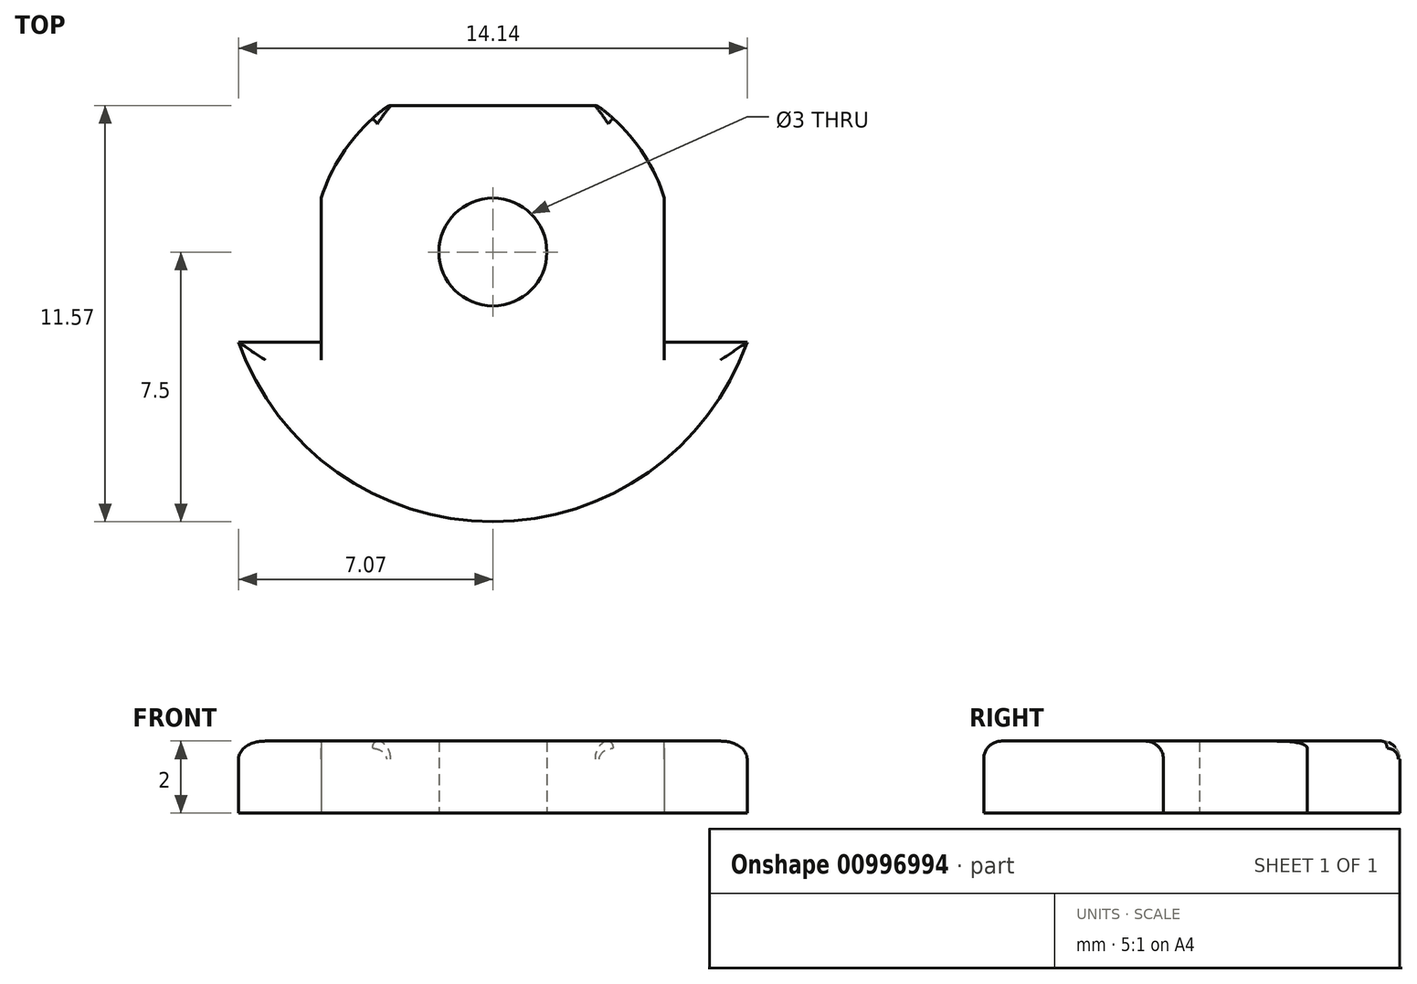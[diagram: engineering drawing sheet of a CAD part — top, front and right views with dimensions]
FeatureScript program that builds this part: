
annotation { "Feature Type Name" : "Feature", "Feature Type Description" : "" }
export const myFeature = defineFeature(function(context is Context, id is Id, definition is map)
    precondition{}
    {
        {
            var Q0;
            Q0=qCreatedBy(makeId("Top.planeOp"),FACE);
            var sketch = newSketch(context, id + "F0", { "sketchPlane" : qUnion([Q0])});
            skCircle(sketch, "E0", {"center": v(0, 0) * mm, "radius": 7.5 * mm});
            skLineSegment(sketch, "E1", {"start": v(-2.7, 7) * mm, "end": v(2.7, 7) * mm});
            skCircle(sketch, "E2", {"center": v(0, 0) * mm, "radius": 5 * mm});
            skLineSegment(sketch, "E3", {"start": v(-2.9, 4.07) * mm, "end": v(2.9, 4.07) * mm});
            skCircle(sketch, "E4", {"center": v(0, 0) * mm, "radius": 1.5 * mm});
            skLineSegment(sketch, "E5", {"start": v(-4.77, 1.5) * mm, "end": v(4.77, 1.5) * mm});
            skLineSegment(sketch, "E6", {"start": v(-7.07, -2.5) * mm, "end": v(7.07, -2.5) * mm});
            skLineSegment(sketch, "E7", {"start": v(-4.77, 1.5) * mm, "end": v(-4.77, -2.5) * mm});
            skLineSegment(sketch, "E8", {"start": v(4.77, 1.5) * mm, "end": v(4.77, -2.5) * mm});
            skSolve(sketch);
        }
        {
            var Q0;
            {var subQ0=sQuery(id+"F0.wireOp",EDGE,"E3");Q0=makeQuery(id+"F0.imprint","IMPRINT",FACE,{"disambiguationData":[TD([[makeQuery(id+"F0.imprint","IMPRINT",EDGE,{"derivedFrom":subQ0}),-1.0]])]});}
            var Q1;
            {var subQ4=sQuery(id+"F0.wireOp",EDGE,"E4");Q1=makeQuery(id+"F0.imprint","IMPRINT",FACE,{"disambiguationData":[TD([[makeQuery(id+"F0.imprint","IMPRINT",EDGE,{"derivedFrom":subQ4}),-1.0]])]});}
            var Q2;
            {var subQ0=sQuery(id+"F0.wireOp",EDGE,"E7");var subQ1=sQuery(id+"F0.wireOp",EDGE,"E2");var subQ2=makeQuery(id+"F0.imprint","INTERSECT",VERTEX,{"derivedFrom":[subQ1,subQ0]});Q2=makeQuery(id+"F0.imprint","IMPRINT",FACE,{"disambiguationData":[TD([[makeQuery(id+"F0.imprint","IMPRINT",EDGE,{"disambiguationData":[TD([[subQ2,-1.0]])],"derivedFrom":subQ1}),-1.0]])]});}
            var Q3;
            {var subQ0=sQuery(id+"F0.wireOp",EDGE,"E6");var subQ1=sQuery(id+"F0.wireOp",EDGE,"E2");var subQ2=makeQuery(id+"F0.imprint","INTERSECT",VERTEX,{"disambiguationData":[OD(0.0)],"derivedFrom":[subQ1,subQ0]});Q3=makeQuery(id+"F0.imprint","IMPRINT",FACE,{"disambiguationData":[TD([[makeQuery(id+"F0.imprint","IMPRINT",EDGE,{"disambiguationData":[TD([[subQ2,-1.0]])],"derivedFrom":subQ1}),1.0]])]});}
            var Q4;
            {var subQ0=sQuery(id+"F0.wireOp",EDGE,"E6");var subQ5=sQuery(id+"F0.wireOp",EDGE,"E0");var subQ8=makeQuery(id+"F0.imprint","INTERSECT",VERTEX,{"disambiguationData":[OD(0.0)],"derivedFrom":[subQ5,subQ0]});Q4=makeQuery(id+"F0.imprint","IMPRINT",FACE,{"disambiguationData":[TD([[makeQuery(id+"F0.imprint","IMPRINT",EDGE,{"disambiguationData":[TD([[subQ8,-1.0]])],"derivedFrom":subQ5}),1.0]])]});}
            var Q5;
            {var subQ0=sQuery(id+"F0.wireOp",EDGE,"E6");var subQ1=sQuery(id+"F0.wireOp",EDGE,"E2");var subQ2=makeQuery(id+"F0.imprint","INTERSECT",VERTEX,{"disambiguationData":[OD(1.0)],"derivedFrom":[subQ1,subQ0]});Q5=makeQuery(id+"F0.imprint","IMPRINT",FACE,{"disambiguationData":[TD([[makeQuery(id+"F0.imprint","IMPRINT",EDGE,{"disambiguationData":[TD([[subQ2,-1.0]])],"derivedFrom":subQ1}),-1.0]])]});}
            extrude(context, id + "F1", {"entities" : qUnion([Q0, Q1, Q2, Q3, Q4, Q5]), "depth" : 2 * mm, "offsetDistance" : 25 * mm});
        }
        {
            var Q0;
            Q0=makeQuery(id+"F1.opExtrude","CAP_EDGE",EDGE,{"disambiguationData":[OSD([sQuery(id+"F0.wireOp",EDGE,"E0")])],"isStart":false});
            var Q1;
            {var subQ0=sQuery(id+"F0.wireOp",EDGE,"E6");Q1=makeQuery(id+"F1.opExtrude","CAP_EDGE",EDGE,{"disambiguationData":[OSD([subQ0]),TDD([makeQuery(id+"F0.imprint","IMPRINT",EDGE,{"disambiguationData":[TD([[makeQuery(id+"F0.imprint","INTERSECT",VERTEX,{"disambiguationData":[OD(0.0)],"derivedFrom":[sQuery(id+"F0.wireOp",EDGE,"E0"),subQ0]}),-1.0]])],"derivedFrom":subQ0})])],"isStart":false});}
            var Q2;
            {var subQ0=sQuery(id+"F0.wireOp",EDGE,"E6");Q2=makeQuery(id+"F1.opExtrude","CAP_EDGE",EDGE,{"disambiguationData":[OSD([subQ0]),TDD([makeQuery(id+"F0.imprint","IMPRINT",EDGE,{"disambiguationData":[TD([[makeQuery(id+"F0.imprint","INTERSECT",VERTEX,{"disambiguationData":[OD(1.0)],"derivedFrom":[sQuery(id+"F0.wireOp",EDGE,"E0"),subQ0]}),1.0]])],"derivedFrom":subQ0})])],"isStart":false});}
            var Q3;
            Q3=makeQuery(id+"F1.opExtrude","CAP_EDGE",EDGE,{"disambiguationData":[OSD([sQuery(id+"F0.wireOp",EDGE,"E3")])],"isStart":false});
            fillet(context, id + "F2", {"entities" : qUnion([Q0, Q1, Q2, Q3]), "radius" : 0.5 * mm, "tangentPropagation" : true, "allowEdgeOverflow" : false});
        }
        {
            var Q0;
            {var subQ0=sQuery(id+"F0.wireOp",EDGE,"E2");Q0=makeQuery(id+"F1.opExtrude","CAP_EDGE",EDGE,{"disambiguationData":[OSD([subQ0]),TDD([makeQuery(id+"F0.imprint","IMPRINT",EDGE,{"disambiguationData":[TD([[makeQuery(id+"F0.imprint","INTERSECT",VERTEX,{"disambiguationData":[OD(0.0)],"derivedFrom":[subQ0,sQuery(id+"F0.wireOp",EDGE,"E3")]}),-1.0]])],"derivedFrom":subQ0})])],"isStart":false});}
            fillet(context, id + "F3", {"entities" : qUnion([Q0]), "radius" : 0.2 * mm, "tangentPropagation" : true, "allowEdgeOverflow" : false});
        }
        {
            var Q0;
            {var subQ0=sQuery(id+"F0.wireOp",EDGE,"E2");Q0=makeQuery(id+"F1.opExtrude","CAP_EDGE",EDGE,{"disambiguationData":[OSD([subQ0]),TDD([makeQuery(id+"F0.imprint","IMPRINT",EDGE,{"disambiguationData":[TD([[makeQuery(id+"F0.imprint","INTERSECT",VERTEX,{"disambiguationData":[OD(1.0)],"derivedFrom":[subQ0,sQuery(id+"F0.wireOp",EDGE,"E3")]}),1.0]])],"derivedFrom":subQ0})])],"isStart":false});}
            fillet(context, id + "F4", {"entities" : qUnion([Q0]), "radius" : 0.2 * mm, "tangentPropagation" : true, "allowEdgeOverflow" : false});
        }
    });
